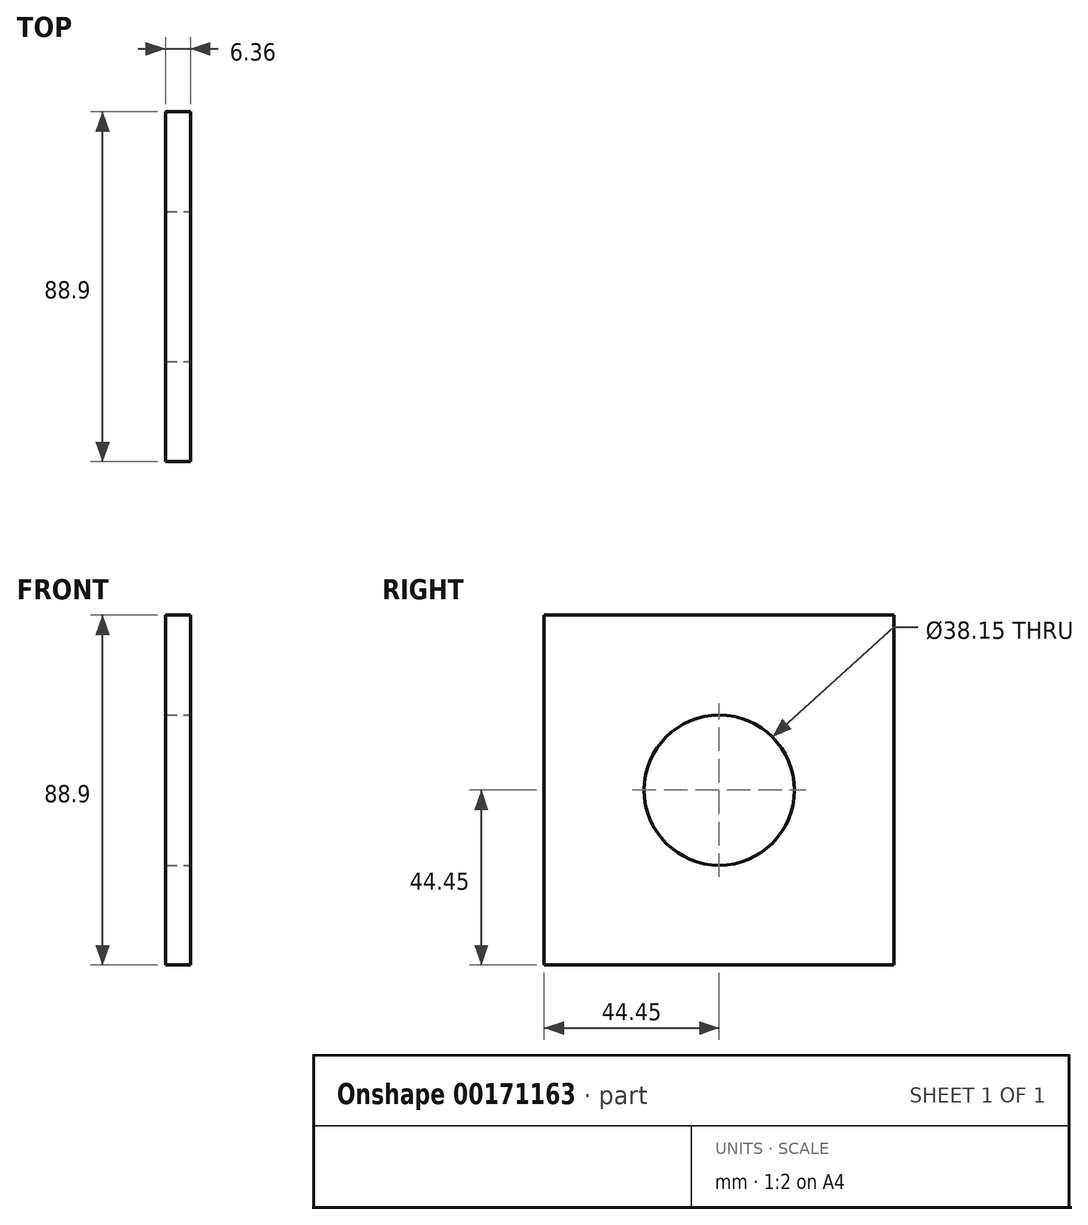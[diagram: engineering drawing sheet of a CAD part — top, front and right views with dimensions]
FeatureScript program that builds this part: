
annotation { "Feature Type Name" : "Feature", "Feature Type Description" : "" }
export const myFeature = defineFeature(function(context is Context, id is Id, definition is map)
    precondition{}
    {
        {
            var Q0;
            Q0=qCreatedBy(makeId("Right.planeOp"),FACE);
            var sketch = newSketch(context, id + "F0", { "sketchPlane" : qUnion([Q0])});
            skLineSegment(sketch, "E0.bottom", {"start": v(-44.45, 44.45) * mm, "end": v(44.45, 44.45) * mm});
            skLineSegment(sketch, "E0.top", {"start": v(-44.45, -44.45) * mm, "end": v(44.45, -44.45) * mm});
            skLineSegment(sketch, "E0.left", {"start": v(-44.45, 44.45) * mm, "end": v(-44.45, -44.45) * mm});
            skLineSegment(sketch, "E0.right", {"start": v(44.45, 44.45) * mm, "end": v(44.45, -44.45) * mm});
            skSolve(sketch);
        }
        {
            var Q0;
            Q0=makeQuery(id+"F0.imprint","IMPRINT",FACE,{"disambiguationData":[TD([[makeQuery(id+"F0.imprint","IMPRINT",EDGE,{"derivedFrom":sQuery(id+"F0.wireOp",EDGE,"E0.bottom")}),-1.0]])]});
            extrude(context, id + "F1", {"entities" : qUnion([Q0]), "depth" : 6.35 * mm, "symmetric" : true});
        }
        {
            var Q0;
            Q0=makeQuery(id+"F1.opExtrude","CAP_FACE",FACE,{"disambiguationData":[OSD([sQuery(id+"F0.wireOp",EDGE,"E0.bottom"),sQuery(id+"F0.wireOp",EDGE,"E0.top"),sQuery(id+"F0.wireOp",EDGE,"E0.left"),sQuery(id+"F0.wireOp",EDGE,"E0.right")])],"isStart":true});
            var sketch = newSketch(context, id + "F2", { "sketchPlane" : qUnion([Q0])});
            skPoint(sketch, "E1", {"position": v(0, 0) * mm});
            skSolve(sketch);
        }
        {
            var Q0;
            Q0=sQuery(id+"F2.wireOp",VERTEX,"E1");
            var Q1;
            Q1=makeQuery(id+"F1.opExtrude","SWEPT_BODY",BODY,{"disambiguationData":[OSD([sQuery(id+"F0.wireOp",EDGE,"E0.bottom"),sQuery(id+"F0.wireOp",EDGE,"E0.top"),sQuery(id+"F0.wireOp",EDGE,"E0.left"),sQuery(id+"F0.wireOp",EDGE,"E0.right")])]});
            hole(context, id + "F3", {"style" : HoleStyle.SIMPLE, "endStyle" : HoleEndStyle.THROUGH, "holeDiameter" : 38.15 * mm, "locations" : qUnion([Q0]), "scope" : qUnion([Q1]), "isTappedThrough" : true});
        }
    });
